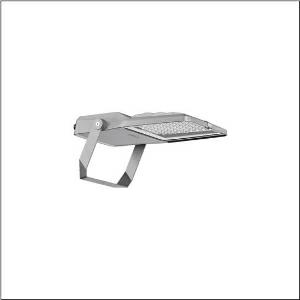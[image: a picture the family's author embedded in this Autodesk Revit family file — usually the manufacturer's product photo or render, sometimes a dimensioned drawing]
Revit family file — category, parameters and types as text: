
# Revit family: floodlight_fl_21_mini___pl61_5xa7773c2c1a_b950
name_source: partatom
category: Lighting Fixtures
units: mm (PartAtom-declared; Revit-internal decimal feet)

## family parameters
Cut with Voids When Loaded = No
Host = Face
Light Source = No
Part Type = Normal
Room Calculation Point = No
Round Connector Dimension = Use Diameter
Shared = No

## types (1)
- --- (1 x LED, 19150 lm, 163.5 W, 3000K)
    Apparent Load = 163 VA
    CIE Flux Codes = 33 65 98 100 100
    Color Rendering = 70
    Color Temperature = 3000K
    Default Elevation = 1800 mm
    Description = Floodlight FL 21 mini, floodlight, primary light control with lens, of PMMA, primary optical cover: protective disc, of toughened safety glass, transparent, light distribution: PL61, light emission: direct distribution, installation type: surface-mounted, LED, High Power LED, rated luminous flux: 19.150lm, luminous efficacy: 117lm/W, light colour: 730, colour temperature: 3000K, control gear: ON/OFF Multilumen, control: Temp-Guard, with terminal, 6-pole, mains connection: 220..240V, AC, 50/60Hz, start of lifetime: 164W, luminaire housing, of diecast aluminium, powder-coated, Siteco® metallic grey (DB 702S), corrosivity category C5 mid according to DIN EN ISO 12944, suitable for swimming pools, chlorine-resistant, sealing non-destructively replaceable, mounting bracket, of steel, galvanised, powder-coated, Siteco® metallic grey (DB 702S), ON/OFF, protection rating (complete): IP66, insulation class (complete): insulation class I (protective earthing), certification: CE, ENEC, VDE, protection symbol: D, impact resistance: IK08, permissible operating ambient temperature: -40..+40°C, permissible operating ambient temperature for outdoor applications: -40..+50°C, standard: DIN EN 12944, LABS conformity tested according to VDMA 24364:2018-05, packaging unit: 1 piece

Light Distribution: PL61
    Height = 70 mm
    Lamp = 1 x LED
    Lamp Light Flux = 19150 lm
    Lamp Power = 163.5 W
    Lamp count = 1
    Length = 485 mm
    Luminous efficacy = 117 lm/W
    Manufacturer = Siteco
    ModVariant = No
    Model = 5XA7773C2C1A
    Number of Poles = 1
    OnlyDefault = Yes
    Power Factor = 1
    Product Name = Floodlight FL 21 mini | PL61
    Product group = floodlight | pylon annexe
    ProductGroupID = 6200
    Protection Class = Protection class I
    Protection Degree = IP 66
    RLX_Detail_Level = 1
    RLX_Emergency_Light_Flux = 0 lm
    RLX_Emergency_Type = 0
    RLX_Emergency_Type_DB = No
    RlxData = <blob elided: 94453 chars, md5=3a328584>
    Socket = socket
    Standby Power = 0 W
    System Light Flux = 19150 lm
    System Power = 163 W
    Type Comments = factory setting: luminous flux: 100 % | (ON | - | - | - | - | - | - | -) | 825 mA
    Type Image = l_1006845.jpg
    URL = http://relux.com
    VarID = @adj_172848
    Voltage = 0 V
    Weight = 0.00 kg
    Width = 337 mm

## geometry (parser evidence)
native form markers: Blend x4, Sweep x13
no freeform markers — native parametric forms only
